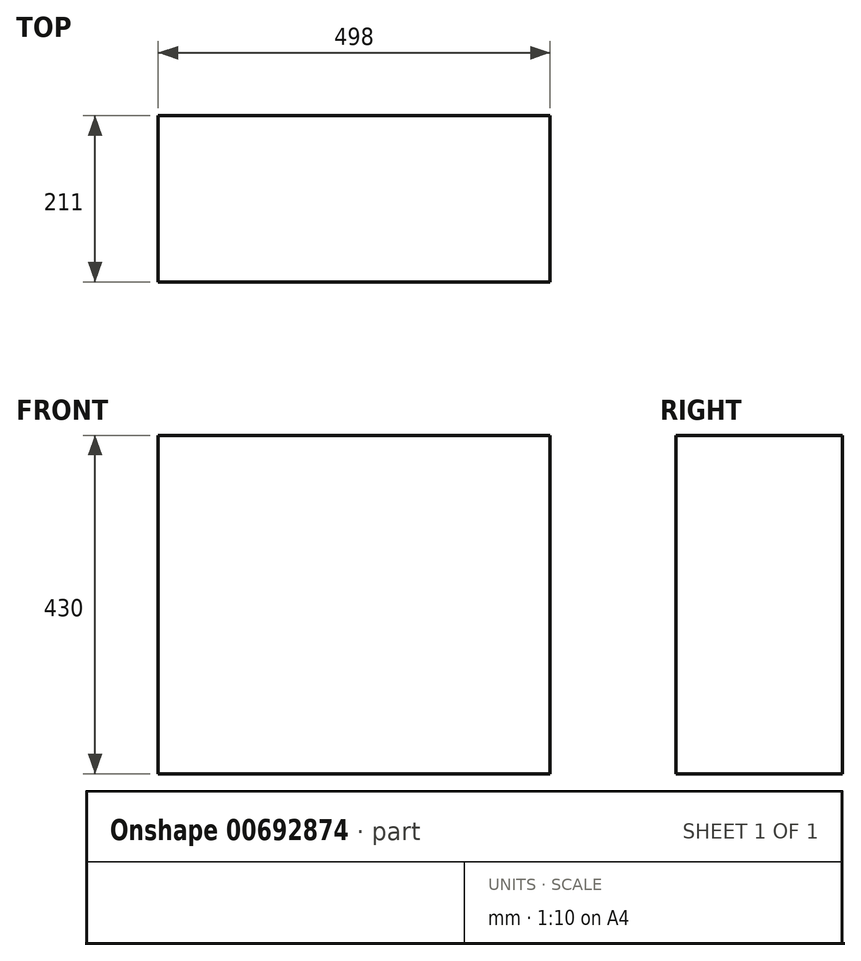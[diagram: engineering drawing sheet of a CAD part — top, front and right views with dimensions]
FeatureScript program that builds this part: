
annotation { "Feature Type Name" : "Feature", "Feature Type Description" : "" }
export const myFeature = defineFeature(function(context is Context, id is Id, definition is map)
    precondition{}
    {
        {
            var Q0;
            Q0=qCreatedBy(makeId("Top.planeOp"),FACE);
            var sketch = newSketch(context, id + "F0", { "sketchPlane" : qUnion([Q0])});
            skLineSegment(sketch, "E0.bottom", {"start": v(249, 105.5) * mm, "end": v(-249, 105.5) * mm});
            skLineSegment(sketch, "E0.top", {"start": v(249, -105.5) * mm, "end": v(-249, -105.5) * mm});
            skLineSegment(sketch, "E0.left", {"start": v(249, 105.5) * mm, "end": v(249, -105.5) * mm});
            skLineSegment(sketch, "E0.right", {"start": v(-249, 105.5) * mm, "end": v(-249, -105.5) * mm});
            skPoint(sketch, "E0.middle", {"position": v(0, 0) * mm});
            skSolve(sketch);
        }
        {
            var Q0;
            Q0 = qSketchRegion(id + "F0", true);
            extrude(context, id + "F1", {"entities" : qUnion([Q0]), "depth" : 430 * mm, "offsetDistance" : 25 * mm});
        }
    });
